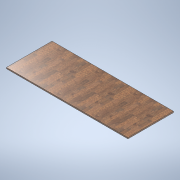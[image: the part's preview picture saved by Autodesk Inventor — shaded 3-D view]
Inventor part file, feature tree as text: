
AUTODESK INVENTOR PART (.ipt)
format: ipt  version: 2020 (Build 240168000, 168)  size: 110,080 bytes
history: native  units: mm
features: extrude x1, sketch x1
ambient origin geometry x8: Origin, YZ Plane, XZ Plane, XY Plane, X Axis, Y Axis, Z Axis, Center Point
bodies: Solid1 (feature_tree)
feature tree (2):
  extrude  "Extrusion1"  Depth=2000.0mm
  sketch  "Sketch1"  dims[d0=750.0mm d1=2000.0mm d2=20.0mm d3=0.0mm]
